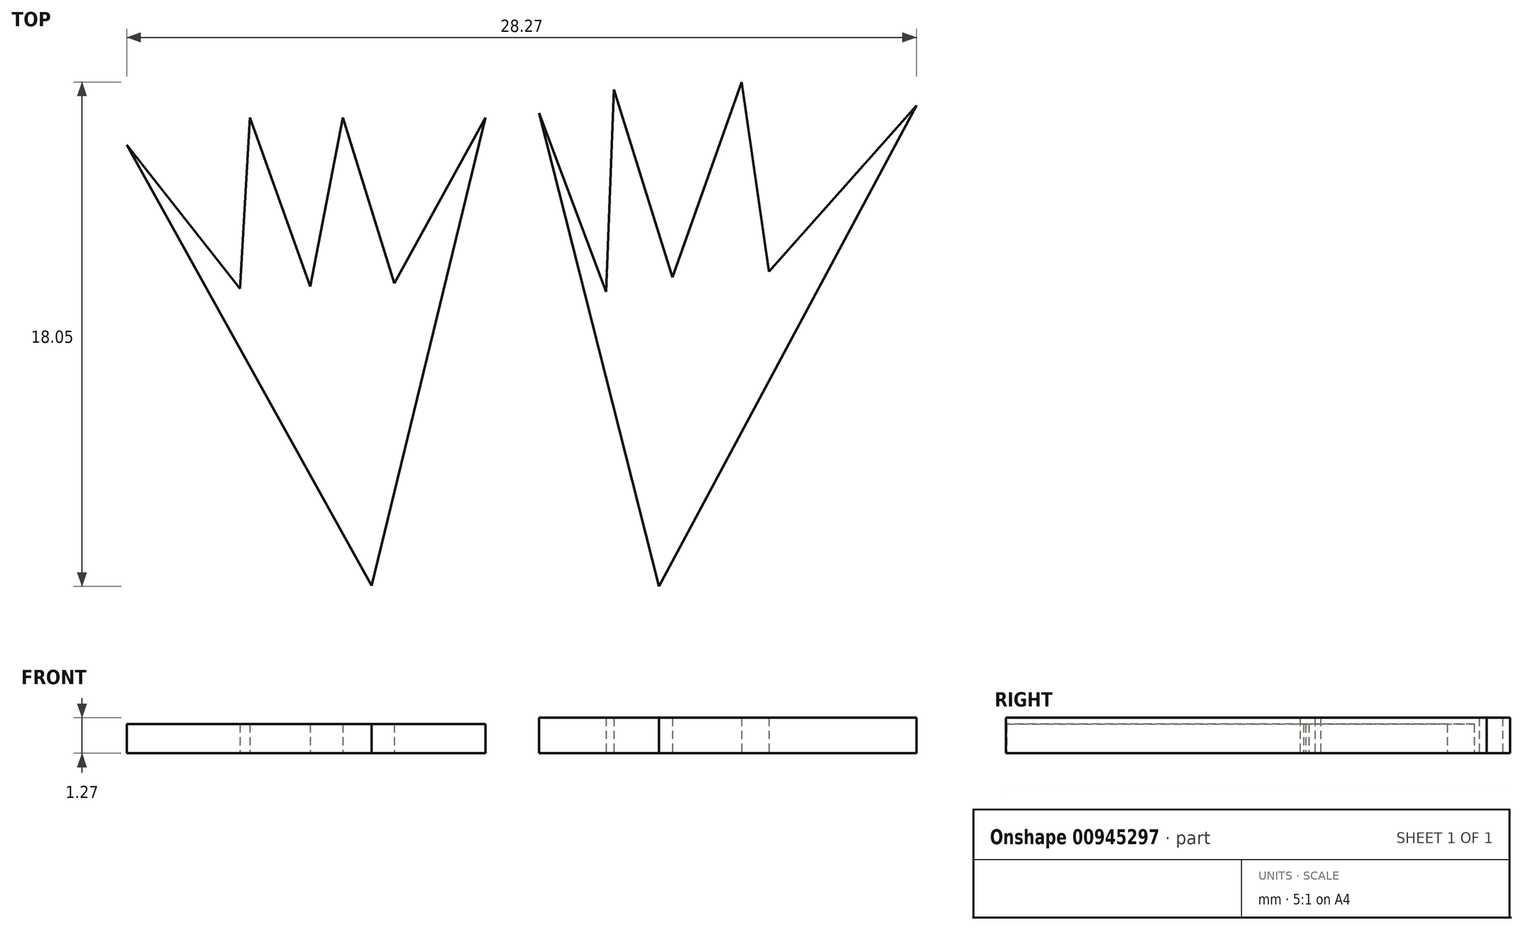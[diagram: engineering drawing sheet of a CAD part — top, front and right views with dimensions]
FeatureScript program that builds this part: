
annotation { "Feature Type Name" : "Feature", "Feature Type Description" : "" }
export const myFeature = defineFeature(function(context is Context, id is Id, definition is map)
    precondition{}
    {
        {
            var Q0;
            Q0=qCreatedBy(makeId("Top.planeOp"),FACE);
            var sketch = newSketch(context, id + "F0", { "sketchPlane" : qUnion([Q0])});
            skLineSegment(sketch, "E0", {"start": v(-44.43, 6.48) * mm, "end": v(-35.67, -9.29) * mm});
            skLineSegment(sketch, "E1", {"start": v(-35.67, -9.29) * mm, "end": v(-31.59, 7.45) * mm});
            skLineSegment(sketch, "E2", {"start": v(-31.59, 7.45) * mm, "end": v(-34.85, 1.53) * mm});
            skLineSegment(sketch, "E3", {"start": v(-34.85, 1.53) * mm, "end": v(-36.69, 7.45) * mm});
            skLineSegment(sketch, "E4", {"start": v(-36.69, 7.45) * mm, "end": v(-37.87, 1.41) * mm});
            skLineSegment(sketch, "E5", {"start": v(-37.87, 1.41) * mm, "end": v(-40.02, 7.45) * mm});
            skLineSegment(sketch, "E6", {"start": v(-40.02, 7.45) * mm, "end": v(-40.38, 1.34) * mm});
            skLineSegment(sketch, "E7", {"start": v(-40.38, 1.34) * mm, "end": v(-44.43, 6.48) * mm});
            skSolve(sketch);
        }
        {
            var Q0;
            Q0 = qSketchRegion(id + "F0", true);
            extrude(context, id + "F1", {"entities" : qUnion([Q0]), "depth" : 1.04 * mm, "offsetDistance" : 25.4 * mm});
        }
        {
            var Q0;
            Q0=qCreatedBy(makeId("Top.planeOp"),FACE);
            var sketch = newSketch(context, id + "F2", { "sketchPlane" : qUnion([Q0])});
            skLineSegment(sketch, "E8", {"start": v(-29.67, 7.62) * mm, "end": v(-25.37, -9.32) * mm});
            skLineSegment(sketch, "E9", {"start": v(-25.37, -9.32) * mm, "end": v(-16.16, 7.9) * mm});
            skLineSegment(sketch, "E10", {"start": v(-16.16, 7.9) * mm, "end": v(-21.44, 1.94) * mm});
            skLineSegment(sketch, "E11", {"start": v(-21.44, 1.94) * mm, "end": v(-22.41, 8.73) * mm});
            skLineSegment(sketch, "E12", {"start": v(-22.41, 8.73) * mm, "end": v(-24.9, 1.74) * mm});
            skLineSegment(sketch, "E13", {"start": v(-24.9, 1.74) * mm, "end": v(-26.98, 8.46) * mm});
            skLineSegment(sketch, "E14", {"start": v(-26.98, 8.46) * mm, "end": v(-27.27, 1.22) * mm});
            skLineSegment(sketch, "E15", {"start": v(-27.27, 1.22) * mm, "end": v(-29.67, 7.62) * mm});
            skSolve(sketch);
        }
        {
            var Q0;
            Q0 = qSketchRegion(id + "F2", true);
            extrude(context, id + "F3", {"entities" : qUnion([Q0]), "depth" : 1.27 * mm, "offsetDistance" : 25.4 * mm});
        }
    });
